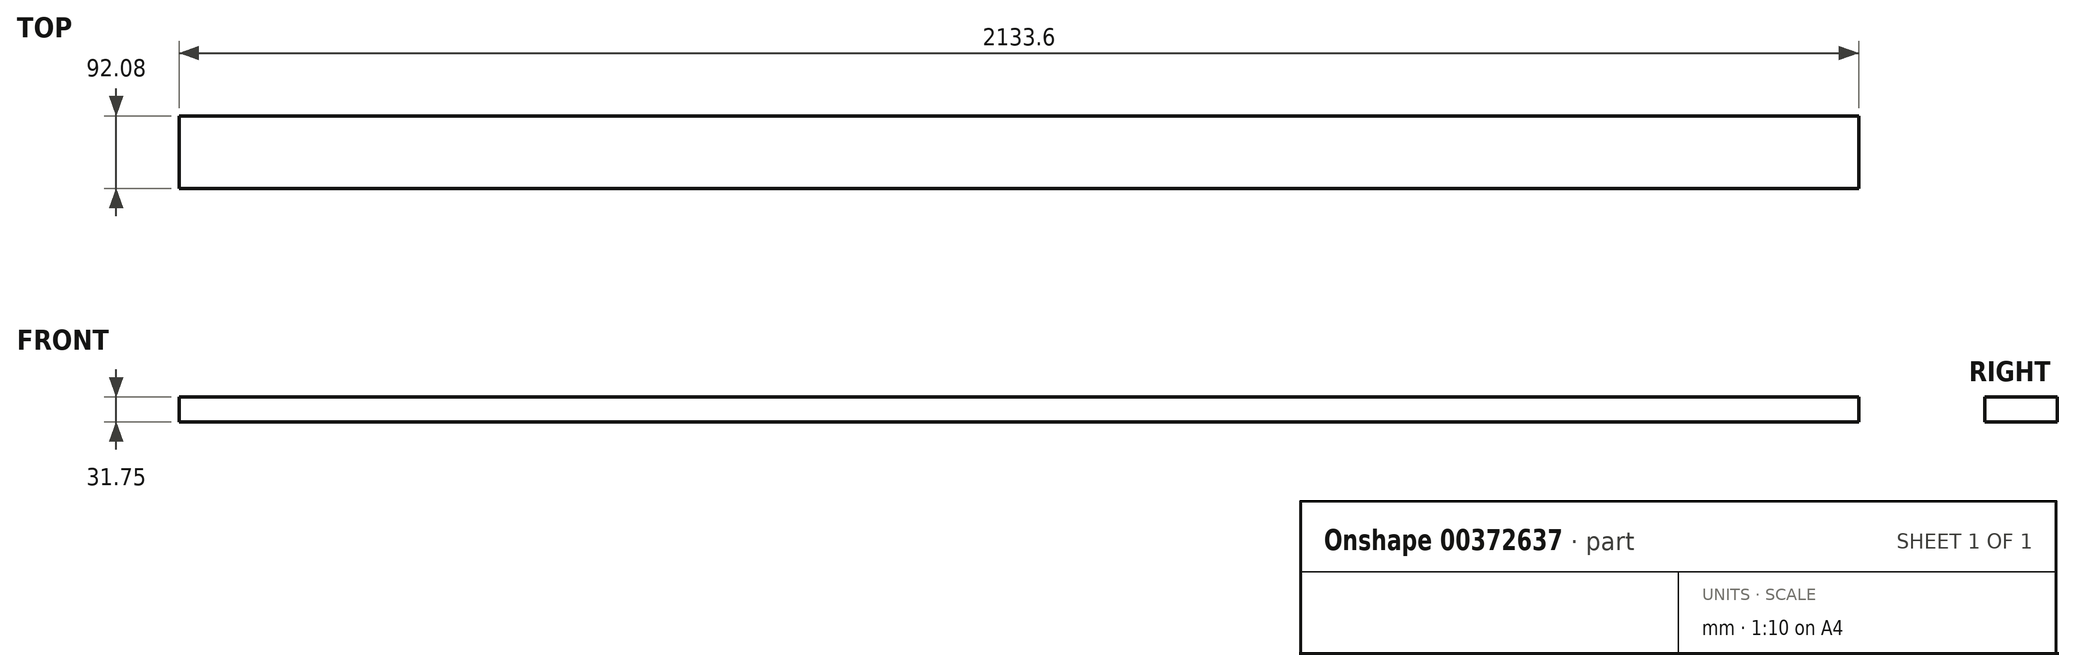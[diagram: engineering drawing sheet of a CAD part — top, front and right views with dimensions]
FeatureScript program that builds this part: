
annotation { "Feature Type Name" : "Feature", "Feature Type Description" : "" }
export const myFeature = defineFeature(function(context is Context, id is Id, definition is map)
    precondition{}
    {
        {
            var Q0;
            Q0=qCreatedBy(makeId("Top.planeOp"),FACE);
            var sketch = newSketch(context, id + "F0", { "sketchPlane" : qUnion([Q0])});
            skLineSegment(sketch, "E0.bottom", {"start": v(-2133.6, 92.07) * mm, "end": v(0, 92.07) * mm});
            skLineSegment(sketch, "E0.top", {"start": v(-2133.6, 0) * mm, "end": v(0, 0) * mm});
            skLineSegment(sketch, "E0.left", {"start": v(-2133.6, 92.07) * mm, "end": v(-2133.6, 0) * mm});
            skLineSegment(sketch, "E0.right", {"start": v(0, 92.07) * mm, "end": v(0, 0) * mm});
            skSolve(sketch);
        }
        {
            var Q0;
            Q0=makeQuery(id+"F0.imprint","IMPRINT",FACE,{"disambiguationData":[TD([[makeQuery(id+"F0.imprint","IMPRINT",EDGE,{"derivedFrom":sQuery(id+"F0.wireOp",EDGE,"E0.bottom")}),-1.0]])]});
            extrude(context, id + "F1", {"entities" : qUnion([Q0]), "depth" : 31.75 * mm});
        }
    });
